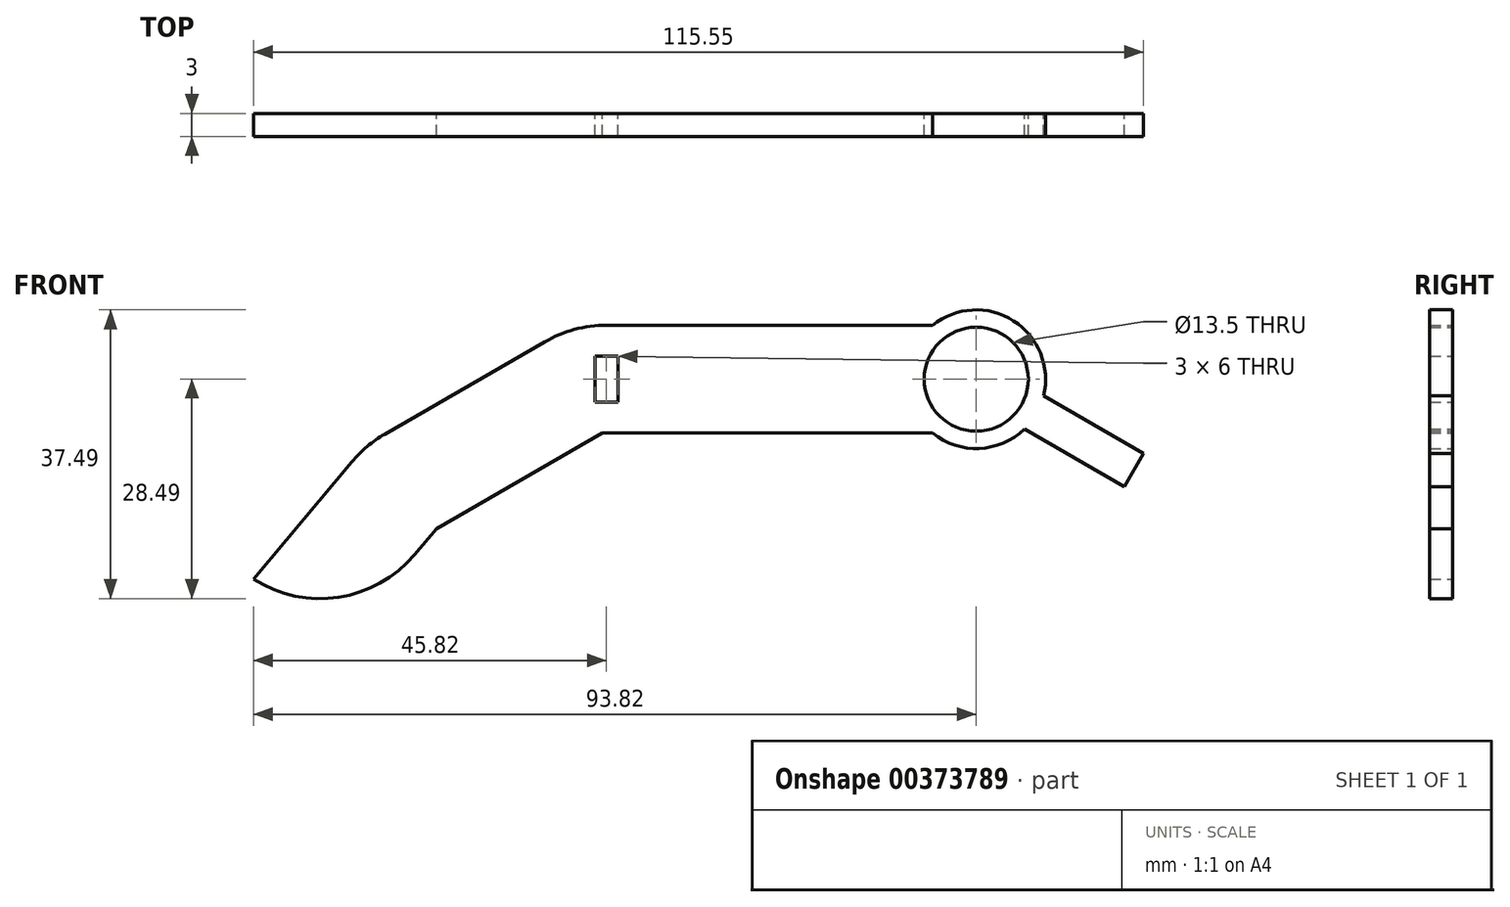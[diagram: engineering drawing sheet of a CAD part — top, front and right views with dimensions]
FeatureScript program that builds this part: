
annotation { "Feature Type Name" : "Feature", "Feature Type Description" : "" }
export const myFeature = defineFeature(function(context is Context, id is Id, definition is map)
    precondition{}
    {
        {
            var Q0;
            Q0=qCreatedBy(makeId("Front.planeOp"),FACE);
            var sketch = newSketch(context, id + "F0", { "sketchPlane" : qUnion([Q0])});
            skLineSegment(sketch, "E0.bottom", {"start": v(24, -9) * mm, "end": v(-24, -9) * mm, "construction": true});
            skLineSegment(sketch, "E0.top", {"start": v(24, 9) * mm, "end": v(-24, 9) * mm, "construction": true});
            skLineSegment(sketch, "E0.left", {"start": v(24, -9) * mm, "end": v(24, 9) * mm, "construction": true});
            skLineSegment(sketch, "E0.right", {"start": v(-24, -9) * mm, "end": v(-24, 9) * mm, "construction": true});
            skPoint(sketch, "E0.middle", {"position": v(0, 0) * mm});
            skArc(sketch, "E1", {"start": v(-24, 9) * mm, "mid": v(-28.66, 8.39) * mm, "end": v(-33, 6.59) * mm, "construction": true});
            skLineSegment(sketch, "E2", {"start": v(-33, 6.59) * mm, "end": v(-24, -9) * mm, "construction": true});
            skLineSegment(sketch, "E3", {"start": v(-33, 6.59) * mm, "end": v(-53.78, -5.41) * mm, "construction": true});
            skLineSegment(sketch, "E4", {"start": v(-24, -9) * mm, "end": v(-44.78, -21) * mm, "construction": true});
            skLineSegment(sketch, "E5", {"start": v(-53.78, -5.41) * mm, "end": v(-44.78, -21) * mm, "construction": true});
            skArc(sketch, "E6", {"start": v(-53.78, -5.41) * mm, "mid": v(-56.35, -7.21) * mm, "end": v(-58.57, -9.43) * mm, "construction": true});
            skLineSegment(sketch, "E7", {"start": v(-58.57, -9.43) * mm, "end": v(-44.78, -21) * mm, "construction": true});
            skLineSegment(sketch, "E8", {"start": v(-58.57, -9.43) * mm, "end": v(-72.71, -26.28) * mm, "construction": true});
            skLineSegment(sketch, "E9", {"start": v(-44.78, -21) * mm, "end": v(-47.36, -24.06) * mm, "construction": true});
            skArc(sketch, "E10", {"start": v(-72.71, -26.28) * mm, "mid": v(-59.58, -30.43) * mm, "end": v(-47.36, -24.06) * mm, "construction": true});
            skCircle(sketch, "E11", {"center": v(24, 0) * mm, "radius": 6.75 * mm});
            skLineSegment(sketch, "E12.0", {"start": v(24, -7) * mm, "end": v(-24.54, -7) * mm, "construction": true});
            skLineSegment(sketch, "E12.1", {"start": v(-24.54, -7) * mm, "end": v(-46.1, -19.44) * mm});
            skLineSegment(sketch, "E12.2", {"start": v(-46.1, -19.44) * mm, "end": v(-48.89, -22.78) * mm});
            skArc(sketch, "E12.3", {"start": v(-69.82, -25.94) * mm, "mid": v(-58.75, -28.31) * mm, "end": v(-48.89, -22.78) * mm});
            skLineSegment(sketch, "E12.4", {"start": v(-57.04, -10.72) * mm, "end": v(-69.82, -25.94) * mm});
            skLineSegment(sketch, "E12.5", {"start": v(24, 7) * mm, "end": v(-24, 7) * mm, "construction": true});
            skArc(sketch, "E12.6", {"start": v(-24, 7) * mm, "mid": v(-28.14, 6.45) * mm, "end": v(-32, 4.86) * mm});
            skLineSegment(sketch, "E12.7", {"start": v(-32, 4.86) * mm, "end": v(-52.78, -7.14) * mm});
            skArc(sketch, "E12.8", {"start": v(-52.78, -7.14) * mm, "mid": v(-55.07, -8.74) * mm, "end": v(-57.04, -10.72) * mm});
            skLineSegment(sketch, "E13", {"start": v(24, -7) * mm, "end": v(24, -9) * mm});
            skLineSegment(sketch, "E14", {"start": v(24, 7) * mm, "end": v(24, 9) * mm});
            skArc(sketch, "E15", {"start": v(24, 9) * mm, "mid": v(21, 8.49) * mm, "end": v(18.34, 7) * mm});
            skArc(sketch, "E16", {"start": v(24, -9) * mm, "mid": v(21, -8.49) * mm, "end": v(18.34, -7) * mm});
            skLineSegment(sketch, "E17", {"start": v(-24.54, -7) * mm, "end": v(18.34, -7) * mm});
            skLineSegment(sketch, "E18", {"start": v(18.34, 7) * mm, "end": v(-24, 7) * mm});
            skArc(sketch, "E19", {"start": v(24, 9) * mm, "mid": v(31.09, 5.55) * mm, "end": v(32.74, -2.16) * mm});
            skArc(sketch, "E20", {"start": v(24, -9) * mm, "mid": v(27.36, -8.35) * mm, "end": v(30.24, -6.49) * mm});
            skLineSegment(sketch, "E21", {"start": v(24, 0) * mm, "end": v(44.48, -11.82) * mm, "construction": true});
            skLineSegment(sketch, "E22", {"start": v(32.74, -2.16) * mm, "end": v(45.73, -9.66) * mm});
            skLineSegment(sketch, "E23", {"start": v(45.73, -9.66) * mm, "end": v(43.23, -13.99) * mm});
            skLineSegment(sketch, "E24", {"start": v(43.23, -13.99) * mm, "end": v(30.24, -6.49) * mm});
            skLineSegment(sketch, "E25.bottom", {"start": v(-22.5, -3) * mm, "end": v(-25.5, -3) * mm});
            skLineSegment(sketch, "E25.top", {"start": v(-22.5, 3) * mm, "end": v(-25.5, 3) * mm});
            skLineSegment(sketch, "E25.left", {"start": v(-22.5, -3) * mm, "end": v(-22.5, 3) * mm});
            skLineSegment(sketch, "E25.right", {"start": v(-25.5, -3) * mm, "end": v(-25.5, 3) * mm});
            skPoint(sketch, "E25.middle", {"position": v(-24, 0) * mm});
            skSolve(sketch);
        }
        {
            var Q0;
            Q0=qSketchRegion(id+"F0",true);
            extrude(context, id + "F1", {"entities" : qUnion([Q0]), "depth" : 3 * mm});
        }
    });
